# Revit family: LUXE-PT
name_source: partatom
category: Generic Models
revit_build: Autodesk Revit Architecture 2012 (Build: 20110309_2315(x64)
units: mm (PartAtom-declared; Revit-internal decimal feet)

## types (1)
- LUXE-PT
    Central Frame Height = 6' - 0"
    Central Frame Width = 2' - 0"
    Material Central Framing = Madix Default
    Material Peg Board = Madix Default
    Q Width = 2' - 7 3/4"
    Q1 Bottom Frame Height = 2' - 6"
    Q1 Footing Depth = 1' - 6"
    Q1 H Frame Width = 1' - 3"
    Q1 Harmonic Grid Material = Madix Default
    Q1 Leg Height = 4' - 6"
    Q1 Leg Material = Madix Default
    Q1 Shelf 1 (on/off) = Yes
    Q1 Shelf 1 Depth = 1' - 6"
    Q1 Shelf 10 (on/off) = Yes
    Q1 Shelf 10 Depth = 1' - 6"
    Q1 Shelf 11 (on/off) = Yes
    Q1 Shelf 11 Depth = 1' - 6"
    Q1 Shelf 12 (on/off) = Yes
    Q1 Shelf 12 Depth = 1' - 6"
    Q1 Shelf 13 (on/off) = Yes
    Q1 Shelf 13 Depth = 1' - 6"
    Q1 Shelf 14 (on/off) = Yes
    Q1 Shelf 14 Depth = 1' - 6"
    Q1 Shelf 15 (on/off) = Yes
    Q1 Shelf 15 Depth = 1' - 6"
    Q1 Shelf 16 (on/off) = Yes
    Q1 Shelf 16 Depth = 1' - 6"
    Q1 Shelf 2 (on/off) = Yes
    Q1 Shelf 2 Depth = 1' - 6"
    Q1 Shelf 3 (on/off) = Yes
    Q1 Shelf 3 Depth = 1' - 6"
    Q1 Shelf 4 (on/off) = Yes
    Q1 Shelf 4 Depth = 1' - 6"
    Q1 Shelf 5 (on/off) = Yes
    Q1 Shelf 5 Depth = 1' - 6"
    Q1 Shelf 6 (on/off) = Yes
    Q1 Shelf 6 Depth = 1' - 6"
    Q1 Shelf 7 (on/off) = Yes
    Q1 Shelf 7 Depth = 1' - 6"
    Q1 Shelf 8 (on/off) = Yes
    Q1 Shelf 8 Depth = 1' - 6"
    Q1 Shelf 9 (on/off) = Yes
    Q1 Shelf 9 Depth = 1' - 6"
    Q1 Shelf Width = 1' - 11"
    Q1 Top Frame Height = 2' - 0"
    Q1 V Frame Width = 1' - 3"
    Q2 Bottom Frame Height = 2' - 6"
    Q2 Footing Depth = 1' - 6"
    Q2 H Frame Width = 1' - 3"
    Q2 Harmonic Grid Material = Madix Default
    Q2 Leg Height = 4' - 6"
    Q2 Leg Material = Madix Default
    Q2 Shelf 1 (on/off) = Yes
    Q2 Shelf 1 Depth = 1' - 6"
    Q2 Shelf 10 (on/off) = Yes
    Q2 Shelf 10 Depth = 1' - 6"
    Q2 Shelf 11 (on/off) = Yes
    Q2 Shelf 11 Depth = 1' - 6"
    Q2 Shelf 12 (on/off) = Yes
    Q2 Shelf 12 Depth = 1' - 6"
    Q2 Shelf 13 (on/off) = Yes
    Q2 Shelf 13 Depth = 1' - 6"
    Q2 Shelf 14 (on/off) = Yes
    Q2 Shelf 14 Depth = 1' - 6"
    Q2 Shelf 15 (on/off) = Yes
    Q2 Shelf 15 Depth = 1' - 6"
    Q2 Shelf 16 (on/off) = Yes
    Q2 Shelf 16 Depth = 1' - 6"
    Q2 Shelf 2 (on/off) = Yes
    Q2 Shelf 2 Depth = 1' - 6"
    Q2 Shelf 3 (on/off) = Yes
    Q2 Shelf 3 Depth = 1' - 6"
    Q2 Shelf 4 (on/off) = Yes
    Q2 Shelf 4 Depth = 1' - 6"
    Q2 Shelf 5 (on/off) = Yes
    Q2 Shelf 5 Depth = 1' - 6"
    Q2 Shelf 6 (on/off) = Yes
    Q2 Shelf 6 Depth = 1' - 6"
    Q2 Shelf 7 (on/off) = Yes
    Q2 Shelf 7 Depth = 1' - 6"
    Q2 Shelf 8 (on/off) = Yes
    Q2 Shelf 8 Depth = 1' - 6"
    Q2 Shelf 9 (on/off) = Yes
    Q2 Shelf 9 Depth = 1' - 6"
    Q2 Shelf Width = 1' - 11"
    Q2 Top Frame Height = 2' - 0"
    Q2 V Frame Width = 1' - 3"
    Q3 Bottom Frame Height = 2' - 6"
    Q3 Depth = 1' - 11 15/32"
    Q3 Footing Depth = 1' - 6"
    Q3 H Frame Width = 1' - 3"
    Q3 Harmonic Grid Material = Madix Default
    Q3 Leg Height = 4' - 6"
    Q3 Leg Material = Madix Default
    Q3 Shelf 01 (on/off) = Yes
    Q3 Shelf 02 (on/off) = Yes
    Q3 Shelf 03 (on/off) = Yes
    Q3 Shelf 04 (on/off) = Yes
    Q3 Shelf 05 (on/off) = Yes
    Q3 Shelf 06 (on/off) = Yes
    Q3 Shelf 07 (on/off) = Yes
    Q3 Shelf 08 (on/off) = Yes
    Q3 Shelf 09 (on/off) = Yes
    Q3 Shelf 1 Depth = 1' - 6"
    Q3 Shelf 10 (on/off) = Yes
    Q3 Shelf 10 Depth = 1' - 6"
    Q3 Shelf 11 (on/off) = Yes
    Q3 Shelf 11 Depth = 1' - 6"
    Q3 Shelf 12 (on/off) = Yes
    Q3 Shelf 12 Depth = 1' - 6"
    Q3 Shelf 13 (on/off) = Yes
    Q3 Shelf 13 Depth = 1' - 6"
    Q3 Shelf 14 (on/off) = Yes
    Q3 Shelf 14 Depth = 1' - 6"
    Q3 Shelf 15 (on/off) = Yes
    Q3 Shelf 15 Depth = 1' - 6"
    Q3 Shelf 16 (on/off) = Yes
    Q3 Shelf 16 Depth = 1' - 6"
    Q3 Shelf 2 Depth = 1' - 6"
    Q3 Shelf 3 Depth = 1' - 6"
    Q3 Shelf 4 Depth = 1' - 6"
    Q3 Shelf 5 Depth = 1' - 6"
    Q3 Shelf 6 Depth = 1' - 6"
    Q3 Shelf 7 Depth = 1' - 6"
    Q3 Shelf 8 Depth = 1' - 6"
    Q3 Shelf 9 Depth = 1' - 6"
    Q3 Shelf Width = 1' - 11"
    Q3 Top Frame Height = 2' - 0"
    Q3 V Frame Width = 1' - 3"
    Q4 Bottom Frame Height = 2' - 6"
    Q4 Footing Depth = 1' - 6"
    Q4 H Frame Width = 1' - 3"
    Q4 Harmonic Grid Material = Madix Default
    Q4 Leg Height = 4' - 6"
    Q4 Leg Material = Madix Default
    Q4 Shelf 1 (on/off) = Yes
    Q4 Shelf 1 Depth = 1' - 6"
    Q4 Shelf 10 (on/off) = Yes
    Q4 Shelf 10 Depth = 1' - 6"
    Q4 Shelf 11 (on/off) = Yes
    Q4 Shelf 11 Depth = 1' - 6"
    Q4 Shelf 12 (on/off) = Yes
    Q4 Shelf 12 Depth = 1' - 6"
    Q4 Shelf 13 (on/off) = Yes
    Q4 Shelf 13 Depth = 1' - 6"
    Q4 Shelf 14 (on/off) = Yes
    Q4 Shelf 14 Depth = 1' - 6"
    Q4 Shelf 15 (on/off) = Yes
    Q4 Shelf 15 Depth = 1' - 6"
    Q4 Shelf 16 (on/off) = Yes
    Q4 Shelf 16 Depth = 1' - 6"
    Q4 Shelf 2 (on/off) = Yes
    Q4 Shelf 2 Depth = 1' - 6"
    Q4 Shelf 3 (on/off) = Yes
    Q4 Shelf 3 Depth = 1' - 6"
    Q4 Shelf 4 (on/off) = Yes
    Q4 Shelf 4 Depth = 1' - 6"
    Q4 Shelf 5 (on/off) = Yes
    Q4 Shelf 5 Depth = 1' - 6"
    Q4 Shelf 6 (on/off) = Yes
    Q4 Shelf 6 Depth = 1' - 6"
    Q4 Shelf 7 (on/off) = Yes
    Q4 Shelf 7 Depth = 1' - 6"
    Q4 Shelf 8 (on/off) = Yes
    Q4 Shelf 8 Depth = 1' - 6"
    Q4 Shelf 9 (on/off) = Yes
    Q4 Shelf 9 Depth = 1' - 6"
    Q4 Shelf Width = 1' - 11"
    Q4 Top Frame Height = 2' - 0"
    Q4 V Frame Width = 1' - 3"
    Shelf A1 (on/off) = Yes
    Shelf A1 Depth = 1' - 6"
    Shelf A10 (on/off) = Yes
    Shelf A10 Depth = 1' - 6"
    Shelf A11 (on/off) = Yes
    Shelf A11 Depth = 1' - 6"
    Shelf A12 (on/off) = Yes
    Shelf A12 Depth = 1' - 6"
    Shelf A13 (on/off) = Yes
    Shelf A13 Depth = 1' - 6"
    Shelf A14 (on/off) = Yes
    Shelf A14 Depth = 1' - 6"
    Shelf A15 (on/off) = Yes
    Shelf A15 Depth = 1' - 6"
    Shelf A16 (on/off) = Yes
    Shelf A16 Depth = 1' - 6"
    Shelf A17 (on/off) = Yes
    Shelf A17 Depth = 1' - 6"
    Shelf A18 (on/off) = Yes
    Shelf A18 Depth = 1' - 6"
    Shelf A2 (on/off) = Yes
    Shelf A2 Depth = 1' - 6"
    Shelf A3 (on/off) = Yes
    Shelf A3 Depth = 1' - 6"
    Shelf A4 (on/off) = Yes
    Shelf A4 Depth = 1' - 6"
    Shelf A5 (on/off) = Yes
    Shelf A5 Depth = 1' - 6"
    Shelf A6 (on/off) = Yes
    Shelf A6 Depth = 1' - 6"
    Shelf A7 (on/off) = Yes
    Shelf A7 Depth = 1' - 6"
    Shelf A8 (on/off) = Yes
    Shelf A8 Depth = 1' - 6"
    Shelf A9 (on/off) = Yes
    Shelf A9 Depth = 1' - 6"
    Shelf Frame Material = Madix Default
    Shelf Material = Madix Default

## geometry (parser evidence)
native form markers: Blend x28, Sweep x152
no freeform markers — native parametric forms only
